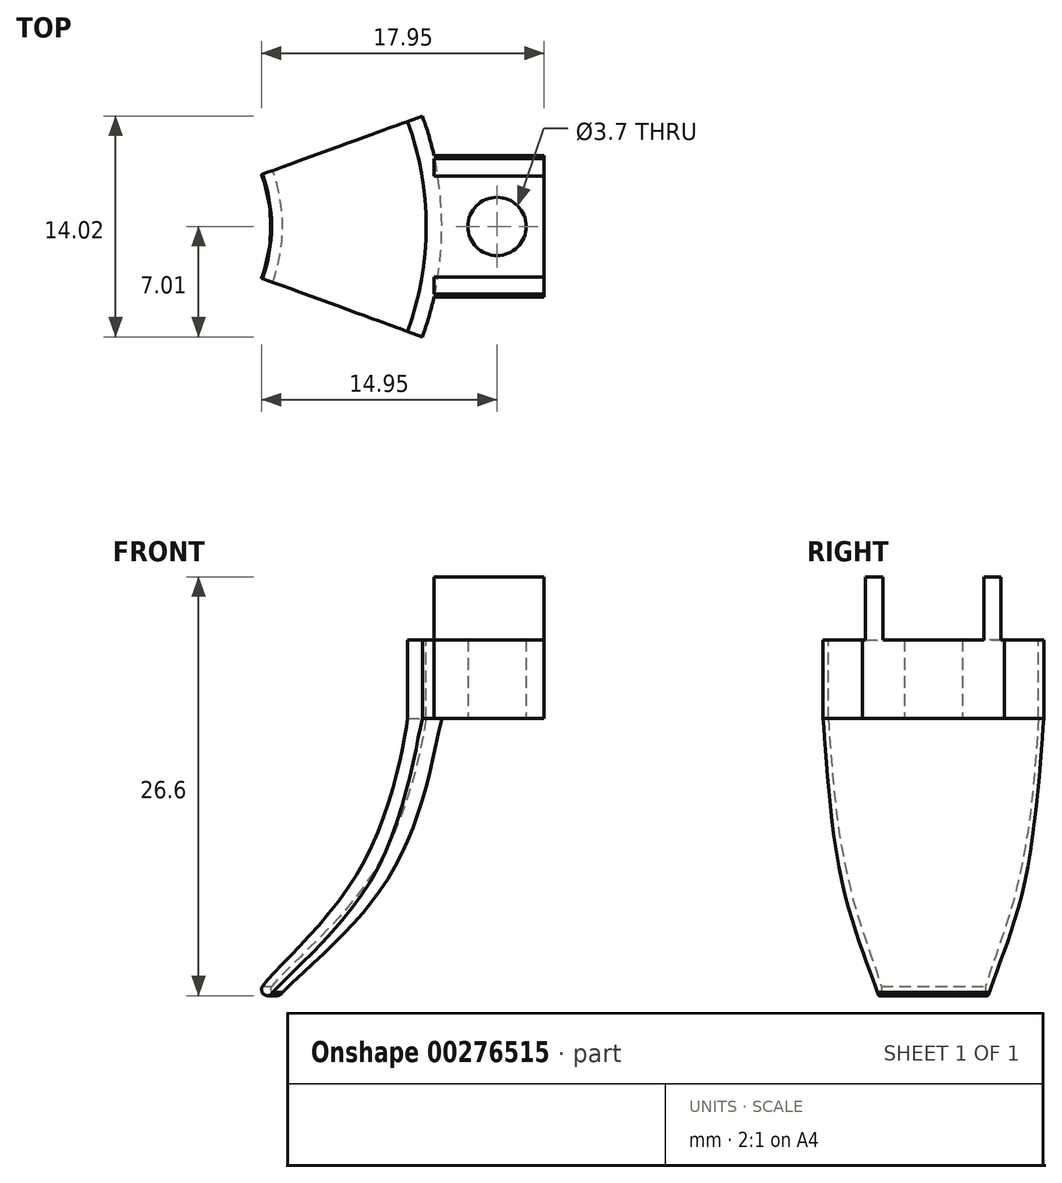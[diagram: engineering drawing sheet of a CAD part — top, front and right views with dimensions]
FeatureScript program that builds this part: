
annotation { "Feature Type Name" : "Feature", "Feature Type Description" : "" }
export const myFeature = defineFeature(function(context is Context, id is Id, definition is map)
    precondition{}
    {
        {
            var Q0;
            Q0=qCreatedBy(makeId("Top.planeOp"),FACE);
            var sketch = newSketch(context, id + "F0", { "sketchPlane" : qUnion([Q0])});
            skLineSegment(sketch, "E0.left", {"start": v(0, 0) * mm, "end": v(0, -9) * mm});
            skLineSegment(sketch, "E0.right", {"start": v(7, 0) * mm, "end": v(7, -9) * mm});
            skLineSegment(sketch, "E1", {"start": v(0, -4.5) * mm, "end": v(7, -4.5) * mm, "construction": true});
            skCircle(sketch, "E2", {"center": v(4, -4.5) * mm, "radius": 1.85 * mm});
            skLineSegment(sketch, "E3", {"start": v(7, -9) * mm, "end": v(0, -9) * mm});
            skLineSegment(sketch, "E4", {"start": v(7, 0) * mm, "end": v(0, 0) * mm});
            skSolve(sketch);
        }
        {
            var Q0;
            Q0=makeQuery(id+"F0.imprint","IMPRINT",FACE,{"disambiguationData":[TD([[makeQuery(id+"F0.imprint","IMPRINT",EDGE,{"derivedFrom":sQuery(id+"F0.wireOp",EDGE,"E0.left")}),1.0]])]});
            extrude(context, id + "F1", {"entities" : qUnion([Q0]), "depth" : 5 * mm});
        }
        {
            var Q0;
            Q0=makeQuery(id+"F1.opExtrude","SWEPT_FACE",FACE,{"disambiguationData":[OSD([sQuery(id+"F0.wireOp",EDGE,"E3")])]});
            cPlane(context, id + "F2", {"entities" : qUnion([Q0]), "cplaneType" : CPlaneType.OFFSET, "offset" : 4.5 * mm, "oppositeDirection" : true, "width" : 150 * mm, "height" : 150 * mm});
        }
        {
            var Q0;
            Q0=qCreatedBy(id+"F2.planeOp",FACE);
            var sketch = newSketch(context, id + "F3", { "sketchPlane" : qUnion([Q0])});
            skLineSegment(sketch, "E5.top", {"start": v(0, 5) * mm, "end": v(-0.5, 5) * mm});
            skLineSegment(sketch, "E5.right", {"start": v(-0.5, 0) * mm, "end": v(-0.5, 5) * mm});
            skLineSegment(sketch, "E6", {"start": v(-0.5, 0) * mm, "end": v(-10.31, -17) * mm, "construction": true});
            skLineSegment(sketch, "E7", {"start": v(-5.4, -8.5) * mm, "end": v(-3.68, -9.5) * mm, "construction": true});
            skFitSpline(sketch, "E8", {"points": [v(-0.5, 0) * mm, v(-3.68, -9.5) * mm, v(-10.31, -17) * mm], "startDerivative": vector(-1.76, -11.23) * mm, "endDerivative": vector(-7.24, -8.77) * mm});
            skLineSegment(sketch, "E9", {"start": v(-3.68, -9.5) * mm, "end": v(-2.8, -10) * mm, "construction": true});
            skLineSegment(sketch, "E10", {"start": v(-10.31, -17) * mm, "end": v(-9.62, -17.4) * mm, "construction": true});
            skArc(sketch, "E11", {"start": v(-10.31, -17) * mm, "mid": v(-10.17, -17.55) * mm, "end": v(-9.62, -17.4) * mm});
            skPoint(sketch, "E11.third.point", {"position": v(-9.62, -17) * mm});
            skFitSpline(sketch, "E12", {"points": [v(-9.62, -17.4) * mm, v(-2.8, -10) * mm, v(0.5, 0) * mm], "startDerivative": vector(7.81, 8.57) * mm, "endDerivative": vector(2.94, 11.98) * mm});
            skLineSegment(sketch, "E13", {"start": v(0.5, 0) * mm, "end": v(0.5, 5) * mm});
            skLineSegment(sketch, "E14", {"start": v(0.5, 5) * mm, "end": v(0, 5) * mm});
            skSolve(sketch);
        }
        {
            var Q0;
            Q0=qCreatedBy(id+"F2.planeOp",FACE);
            var sketch = newSketch(context, id + "F4", { "sketchPlane" : qUnion([Q0])});
            skLineSegment(sketch, "E15", {"start": v(0, 2.5) * mm, "end": v(-20, 2.5) * mm, "construction": true});
            skLineSegment(sketch, "E16", {"start": v(-20, 2.5) * mm, "end": v(-20, 0.36) * mm, "construction": true});
            skSolve(sketch);
        }
        {
            var Q0;
            Q0 = qSketchRegion(id + "F3", true);
            var Q1;
            Q1=sQuery(id+"F4.wireOp",EDGE,"E16");
            revolve(context, id + "F5", {"operationType" : NewBodyOperationType.ADD, "entities" : qUnion([Q0]), "axis" : qUnion([Q1]), "revolveType" : RevolveType.TWO_DIRECTIONS, "angle" : 20 * degree, "angleBack" : 340 * degree});
        }
        {
            var Q0;
            Q0=makeQuery(id+"F5.boolean.opBoolean","MERGE",FACE,{"derivedFrom":[makeQuery(id+"F1.opExtrude","CAP_FACE",FACE,{"disambiguationData":[OSD([sQuery(id+"F0.wireOp",EDGE,"E0.top"),sQuery(id+"F0.wireOp",EDGE,"E0.left"),sQuery(id+"F0.wireOp",EDGE,"E0.right"),sQuery(id+"F0.wireOp",EDGE,"jq0kd9at-NIws-fKRg-i4rP-gFyy0y6J2BYD.top"),sQuery(id+"F0.wireOp",EDGE,"jq0kd9at-NIws-fKRg-i4rP-gFyy0y6J2BYD.left"),sQuery(id+"F0.wireOp",EDGE,"jq0kd9at-NIws-fKRg-i4rP-gFyy0y6J2BYD.right"),sQuery(id+"F0.wireOp",EDGE,"aa351be9-c543-416d-b4e2-9337366d5d7e.trimOffspring"),sQuery(id+"F0.wireOp",EDGE,"3878a35b-c340-41f7-b40b-085ad4daaa9f0.MirrorCS"),sQuery(id+"F0.wireOp",EDGE,"3878a35b-c340-41f7-b40b-085ad4daaa9f1.MirrorCS"),sQuery(id+"F0.wireOp",EDGE,"3878a35b-c340-41f7-b40b-085ad4daaa9f2.MirrorCS"),sQuery(id+"F0.wireOp",EDGE,"3878a35b-c340-41f7-b40b-085ad4daaa9f3.MirrorCS"),sQuery(id+"F0.wireOp",EDGE,"3878a35b-c340-41f7-b40b-085ad4daaa9f4.MirrorCS"),sQuery(id+"F0.wireOp",EDGE,"E2")])],"isStart":false}),makeQuery(id+"F5.opRevolve","SWEPT_FACE",FACE,{"disambiguationData":[OSD([sQuery(id+"F3.wireOp",EDGE,"E5.top"),sQuery(id+"F3.wireOp",EDGE,"E14")])]})]});
            var sketch = newSketch(context, id + "F6", { "sketchPlane" : qUnion([Q0])});
            skLineSegment(sketch, "E17", {"start": v(1.6, 0) * mm, "end": v(0, 0) * mm});
            skLineSegment(sketch, "E18", {"start": v(0, 0) * mm, "end": v(0, 10) * mm});
            skLineSegment(sketch, "E19", {"start": v(0, 10) * mm, "end": v(1.6, 10) * mm});
            skLineSegment(sketch, "E20", {"start": v(1.6, 10) * mm, "end": v(1.6, 0) * mm});
            skLineSegment(sketch, "E21", {"start": v(1.6, -9) * mm, "end": v(0, -9) * mm});
            skLineSegment(sketch, "E22", {"start": v(0, -9) * mm, "end": v(0, -10.87) * mm});
            skLineSegment(sketch, "E23", {"start": v(0, -10.87) * mm, "end": v(1.6, -10.87) * mm});
            skLineSegment(sketch, "E24", {"start": v(1.6, -10.87) * mm, "end": v(1.6, -9) * mm});
            skSolve(sketch);
        }
        {
            var Q0;
            {var subQ0=sQuery(id+"F6.wireOp",EDGE,"E21");var subQ6=sQuery(id+"F6.wireOp",EDGE,"E22");var subQ7=makeQuery(id+"F6.imprint","INTERSECT",VERTEX,{"derivedFrom":[subQ0,subQ6]});Q0=makeQuery(id+"F6.imprint","IMPRINT",FACE,{"disambiguationData":[TD([[makeQuery(id+"F6.imprint","IMPRINT",EDGE,{"disambiguationData":[TD([[subQ7,-1.0]])],"derivedFrom":subQ6}),1.0]])]});}
            var Q1;
            {var subQ0=sQuery(id+"F6.wireOp",EDGE,"E17");var subQ6=sQuery(id+"F6.wireOp",EDGE,"E18");var subQ7=makeQuery(id+"F6.imprint","INTERSECT",VERTEX,{"derivedFrom":[subQ0,subQ6]});Q1=makeQuery(id+"F6.imprint","IMPRINT",FACE,{"disambiguationData":[TD([[makeQuery(id+"F6.imprint","IMPRINT",EDGE,{"disambiguationData":[TD([[subQ7,-1.0]])],"derivedFrom":subQ6}),-1.0]])]});}
            extrude(context, id + "F7", {"entities" : qUnion([Q0, Q1]), "operationType" : NewBodyOperationType.REMOVE, "oppositeDirection" : true, "depth" : 5 * mm});
        }
        {
            var Q0;
            Q0=makeQuery(id+"F5.boolean.opBoolean","MERGE",FACE,{"derivedFrom":[makeQuery(id+"F1.opExtrude","CAP_FACE",FACE,{"disambiguationData":[OSD([sQuery(id+"F0.wireOp",EDGE,"E0.left"),sQuery(id+"F0.wireOp",EDGE,"E0.right"),sQuery(id+"F0.wireOp",EDGE,"E2"),sQuery(id+"F0.wireOp",EDGE,"E3"),sQuery(id+"F0.wireOp",EDGE,"E4")])],"isStart":false}),makeQuery(id+"F5.opRevolve","SWEPT_FACE",FACE,{"disambiguationData":[OSD([sQuery(id+"F3.wireOp",EDGE,"E5.top"),sQuery(id+"F3.wireOp",EDGE,"E14")])]})]});
            var sketch = newSketch(context, id + "F8", { "sketchPlane" : qUnion([Q0])});
            skLineSegment(sketch, "E25.bottom", {"start": v(7, 0) * mm, "end": v(0, 0) * mm});
            skLineSegment(sketch, "E25.top", {"start": v(7, -1.5) * mm, "end": v(0, -1.5) * mm});
            skLineSegment(sketch, "E25.left", {"start": v(7, 0) * mm, "end": v(7, -1.5) * mm});
            skLineSegment(sketch, "E25.right", {"start": v(0, 0) * mm, "end": v(0, -1.5) * mm});
            skLineSegment(sketch, "E26.bottom", {"start": v(7, -9) * mm, "end": v(0, -9) * mm});
            skLineSegment(sketch, "E26.top", {"start": v(7, -7.5) * mm, "end": v(0, -7.5) * mm});
            skLineSegment(sketch, "E26.left", {"start": v(7, -9) * mm, "end": v(7, -7.5) * mm});
            skLineSegment(sketch, "E26.right", {"start": v(0, -9) * mm, "end": v(0, -7.5) * mm});
            skSolve(sketch);
        }
        {
            var Q0;
            Q0=makeQuery(id+"F8.imprint","IMPRINT",FACE,{"disambiguationData":[TD([[makeQuery(id+"F8.imprint","IMPRINT",EDGE,{"derivedFrom":sQuery(id+"F8.wireOp",EDGE,"E25.bottom")}),1.0]])]});
            var Q1;
            Q1=makeQuery(id+"F8.imprint","IMPRINT",FACE,{"disambiguationData":[TD([[makeQuery(id+"F8.imprint","IMPRINT",EDGE,{"derivedFrom":sQuery(id+"F8.wireOp",EDGE,"E26.bottom")}),-1.0]])]});
            extrude(context, id + "F9", {"entities" : qUnion([Q0, Q1]), "operationType" : NewBodyOperationType.ADD, "depth" : 4 * mm});
        }
        {
            var Q0;
            Q0=makeQuery(id+"F9.boolean.opBoolean","MERGE",FACE,{"derivedFrom":[makeQuery(id+"F1.opExtrude","SWEPT_FACE",FACE,{"disambiguationData":[OSD([sQuery(id+"F0.wireOp",EDGE,"E0.right")])]}),makeQuery(id+"F9.opExtrude","SWEPT_FACE",FACE,{"disambiguationData":[OSD([sQuery(id+"F8.wireOp",EDGE,"E25.left")])]}),makeQuery(id+"F9.opExtrude","SWEPT_FACE",FACE,{"disambiguationData":[OSD([sQuery(id+"F8.wireOp",EDGE,"E26.left")])]})]});
            var sketch = newSketch(context, id + "F10", { "sketchPlane" : qUnion([Q0])});
            skLineSegment(sketch, "E27", {"start": v(-7.5, 5) * mm, "end": v(-7.7, 5) * mm});
            skLineSegment(sketch, "E28", {"start": v(-7.7, 5) * mm, "end": v(-7.7, 9) * mm});
            skLineSegment(sketch, "E29.0", {"start": v(-7.5, 9) * mm, "end": v(-7.7, 9) * mm});
            skLineSegment(sketch, "E30", {"start": v(-8.25, 9) * mm, "end": v(-8.25, 6) * mm, "construction": true});
            skLineSegment(sketch, "E31.MirrorCS", {"start": v(-8.8, 5) * mm, "end": v(-8.8, 9) * mm});
            skLineSegment(sketch, "E32.MirrorCS", {"start": v(-9, 5) * mm, "end": v(-8.8, 5) * mm});
            skLineSegment(sketch, "E33.0", {"start": v(-7.5, 9) * mm, "end": v(-7.5, 5) * mm});
            skLineSegment(sketch, "E34.0", {"start": v(-9, 9) * mm, "end": v(-9, 5) * mm});
            skPoint(sketch, "E35.orphan", {"position": v(-9, 0) * mm});
            skLineSegment(sketch, "E36.trimOffspring", {"start": v(-8.8, 9) * mm, "end": v(-9, 9) * mm});
            skLineSegment(sketch, "E37.MirrorCS", {"start": v(-9, 9) * mm, "end": v(-8.8, 9) * mm});
            skLineSegment(sketch, "E38.MirrorCS", {"start": v(-7.7, 9) * mm, "end": v(-7.5, 9) * mm});
            skLineSegment(sketch, "E39", {"start": v(-4.5, 5) * mm, "end": v(-4.5, 7.43) * mm, "construction": true});
            skLineSegment(sketch, "E40.MirrorCS", {"start": v(-0.2, 9) * mm, "end": v(0, 9) * mm});
            skLineSegment(sketch, "E41.MirrorCS", {"start": v(0, 5) * mm, "end": v(-0.2, 5) * mm});
            skLineSegment(sketch, "E42.MirrorCS", {"start": v(0, 9) * mm, "end": v(0, 5) * mm});
            skLineSegment(sketch, "E43.MirrorCS", {"start": v(-0.2, 5) * mm, "end": v(-0.2, 9) * mm});
            skLineSegment(sketch, "E44.MirrorCS", {"start": v(-1.5, 9) * mm, "end": v(-1.3, 9) * mm});
            skLineSegment(sketch, "E45.MirrorCS", {"start": v(-1.5, 9) * mm, "end": v(-1.5, 5) * mm});
            skLineSegment(sketch, "E46.MirrorCS", {"start": v(-1.3, 5) * mm, "end": v(-1.3, 9) * mm});
            skLineSegment(sketch, "E47.MirrorCS", {"start": v(-1.5, 5) * mm, "end": v(-1.3, 5) * mm});
            skSolve(sketch);
        }
        {
            var Q0;
            Q0 = qSketchRegion(id + "F10", true);
            extrude(context, id + "F11", {"entities" : qUnion([Q0]), "operationType" : NewBodyOperationType.REMOVE, "oppositeDirection" : true, "depth" : 25 * mm});
        }
    });
